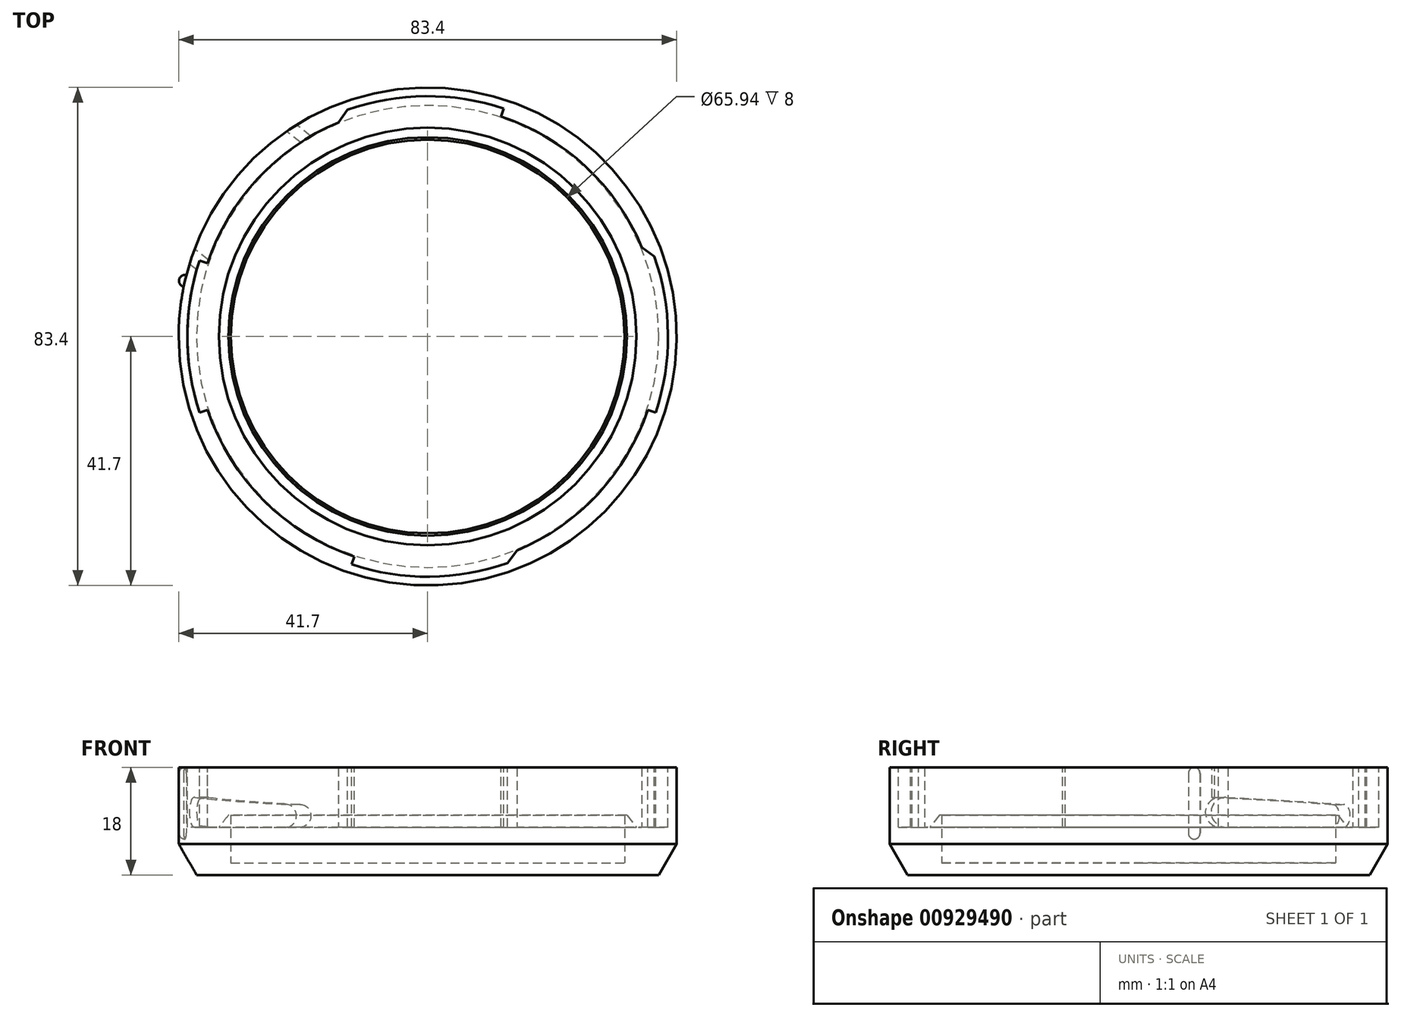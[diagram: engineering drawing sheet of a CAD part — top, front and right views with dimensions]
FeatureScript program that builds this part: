
annotation { "Feature Type Name" : "Feature", "Feature Type Description" : "" }
export const myFeature = defineFeature(function(context is Context, id is Id, definition is map)
    precondition{}
    {
        {
            var Q0;
            Q0=qCreatedBy(makeId("Front.planeOp"),FACE);
            var sketch = newSketch(context, id + "F0", { "sketchPlane" : qUnion([Q0])});
            skLineSegment(sketch, "E0", {"start": v(0, 0) * mm, "end": v(41.7, 0) * mm});
            skLineSegment(sketch, "E1", {"start": v(0, 0) * mm, "end": v(0, 2) * mm});
            skLineSegment(sketch, "E2", {"start": v(41.7, 0) * mm, "end": v(41.7, 18) * mm});
            skLineSegment(sketch, "E3", {"start": v(41.7, 18) * mm, "end": v(38.85, 18) * mm});
            skLineSegment(sketch, "E4", {"start": v(38.85, 18) * mm, "end": v(38.85, 8) * mm});
            skLineSegment(sketch, "E5", {"start": v(38.85, 8) * mm, "end": v(34.97, 8) * mm});
            skLineSegment(sketch, "E6", {"start": v(34.97, 8) * mm, "end": v(34.97, 10) * mm});
            skLineSegment(sketch, "E7", {"start": v(34.97, 10) * mm, "end": v(32.97, 10) * mm});
            skLineSegment(sketch, "E8", {"start": v(32.97, 10) * mm, "end": v(32.97, 2) * mm});
            skLineSegment(sketch, "E9", {"start": v(32.97, 2) * mm, "end": v(0, 2) * mm});
            skLineSegment(sketch, "E10", {"start": v(0, 2) * mm, "end": v(0, 44.08) * mm, "construction": true});
            skSolve(sketch);
        }
        {
            var Q0;
            Q0 = qSketchRegion(id + "F0", true);
            var Q1;
            Q1=sQuery(id+"F0.wireOp",EDGE,"E1");
            revolve(context, id + "F1", {"surfaceOperationType" : NewSurfaceOperationType.NEW, "entities" : qUnion([Q0]), "axis" : qUnion([Q1]), "revolveType" : RevolveType.FULL});
        }
        {
            var Q0;
            Q0=makeQuery(id+"F1.opRevolve","SWEPT_FACE",FACE,{"disambiguationData":[OSD([sQuery(id+"F0.wireOp",EDGE,"E3")])]});
            var sketch = newSketch(context, id + "F2", { "sketchPlane" : qUnion([Q0])});
            skPoint(sketch, "E11.center", {"position": v(0, 0) * mm});
            skArc(sketch, "E12.trimOffspring", {"start": v(12.73, 38.18) * mm, "mid": v(0, 40.25) * mm, "end": v(-12.73, 38.18) * mm});
            skArc(sketch, "E13.1.0", {"start": v(38.18, -12.73) * mm, "mid": v(40.25, 0) * mm, "end": v(38.18, 12.73) * mm});
            skArc(sketch, "E13.2.0", {"start": v(-12.73, -38.18) * mm, "mid": v(0, -40.25) * mm, "end": v(12.73, -38.18) * mm});
            skArc(sketch, "E13.3.0", {"start": v(-38.18, 12.73) * mm, "mid": v(-40.25, 0) * mm, "end": v(-38.18, -12.73) * mm});
            skLineSegment(sketch, "E14", {"start": v(12.73, 38.18) * mm, "end": v(12.29, 36.86) * mm});
            skLineSegment(sketch, "E15", {"start": v(-12.73, 38.18) * mm, "end": v(-12.29, 36.86) * mm});
            skLineSegment(sketch, "E16", {"start": v(38.18, 12.73) * mm, "end": v(36.86, 12.29) * mm});
            skLineSegment(sketch, "E17", {"start": v(38.18, -12.73) * mm, "end": v(36.86, -12.29) * mm});
            skArc(sketch, "E18", {"start": v(12.29, 36.86) * mm, "mid": v(0, 38.85) * mm, "end": v(-12.29, 36.86) * mm});
            skArc(sketch, "E19", {"start": v(-12.29, 36.86) * mm, "mid": v(-27.47, 27.47) * mm, "end": v(-36.86, 12.29) * mm});
            skArc(sketch, "E20", {"start": v(-36.86, 12.29) * mm, "mid": v(-38.85, 0) * mm, "end": v(-36.86, -12.29) * mm});
            skArc(sketch, "E21", {"start": v(-36.86, -12.29) * mm, "mid": v(-27.47, -27.47) * mm, "end": v(-12.29, -36.86) * mm});
            skArc(sketch, "E22", {"start": v(-12.29, -36.86) * mm, "mid": v(0, -38.85) * mm, "end": v(12.29, -36.86) * mm});
            skArc(sketch, "E23", {"start": v(12.29, -36.86) * mm, "mid": v(27.47, -27.47) * mm, "end": v(36.86, -12.29) * mm});
            skArc(sketch, "E24", {"start": v(36.86, -12.29) * mm, "mid": v(38.85, 0) * mm, "end": v(36.86, 12.29) * mm});
            skArc(sketch, "E25", {"start": v(36.86, 12.29) * mm, "mid": v(27.47, 27.47) * mm, "end": v(12.29, 36.86) * mm});
            skLineSegment(sketch, "E26", {"start": v(12.29, -36.86) * mm, "end": v(12.73, -38.18) * mm});
            skLineSegment(sketch, "E27", {"start": v(-12.29, -36.86) * mm, "end": v(-12.73, -38.18) * mm});
            skLineSegment(sketch, "E28", {"start": v(-36.86, -12.29) * mm, "end": v(-38.18, -12.73) * mm});
            skLineSegment(sketch, "E29", {"start": v(-36.86, 12.29) * mm, "end": v(-38.18, 12.73) * mm});
            skSolve(sketch);
        }
        {
            var Q0;
            Q0=makeQuery(id+"F2.imprint","IMPRINT",FACE,{"disambiguationData":[TD([[makeQuery(id+"F2.imprint","IMPRINT",EDGE,{"derivedFrom":sQuery(id+"F2.wireOp",EDGE,"E12.trimOffspring")}),1.0]])]});
            var Q1;
            Q1=makeQuery(id+"F2.imprint","IMPRINT",FACE,{"disambiguationData":[TD([[makeQuery(id+"F2.imprint","IMPRINT",EDGE,{"derivedFrom":sQuery(id+"F2.wireOp",EDGE,"E13.1.0")}),1.0]])]});
            var Q2;
            Q2=makeQuery(id+"F2.imprint","IMPRINT",FACE,{"disambiguationData":[TD([[makeQuery(id+"F2.imprint","IMPRINT",EDGE,{"derivedFrom":sQuery(id+"F2.wireOp",EDGE,"E13.2.0")}),1.0]])]});
            var Q3;
            Q3=makeQuery(id+"F2.imprint","IMPRINT",FACE,{"disambiguationData":[TD([[makeQuery(id+"F2.imprint","IMPRINT",EDGE,{"derivedFrom":sQuery(id+"F2.wireOp",EDGE,"E13.3.0")}),1.0]])]});
            var Q4;
            Q4=makeQuery(id+"F1.opRevolve","SWEPT_FACE",FACE,{"disambiguationData":[OSD([sQuery(id+"F0.wireOp",EDGE,"E5")])]});
            extrude(context, id + "F3", {"entities" : qUnion([Q0, Q1, Q2, Q3]), "operationType" : NewBodyOperationType.REMOVE, "endBound" : BoundingType.UP_TO_SURFACE, "oppositeDirection" : true, "depth" : 10 * mm, "endBoundEntityFace" : qUnion([Q4]), "offsetDistance" : 25 * mm});
        }
        {
            var Q0;
            Q0=makeQuery(id+"F3.boolean.opBoolean","COPY",EDGE,{"derivedFrom":makeQuery(id+"F3.opExtrude","SWEPT_EDGE",EDGE,{"disambiguationData":[OSD([sQuery(id+"F2.wireOp",EDGE,"E16"),sQuery(id+"F2.wireOp",EDGE,"E24"),sQuery(id+"F2.wireOp",EDGE,"E25")])]})});
            var Q1;
            Q1=makeQuery(id+"F3.boolean.opBoolean","COPY",EDGE,{"derivedFrom":makeQuery(id+"F3.opExtrude","SWEPT_EDGE",EDGE,{"disambiguationData":[OSD([sQuery(id+"F2.wireOp",EDGE,"E15"),sQuery(id+"F2.wireOp",EDGE,"E18"),sQuery(id+"F2.wireOp",EDGE,"E19")])]})});
            var Q2;
            Q2=makeQuery(id+"F3.boolean.opBoolean","COPY",EDGE,{"derivedFrom":makeQuery(id+"F3.opExtrude","SWEPT_EDGE",EDGE,{"disambiguationData":[OSD([sQuery(id+"F2.wireOp",EDGE,"E22"),sQuery(id+"F2.wireOp",EDGE,"E23"),sQuery(id+"F2.wireOp",EDGE,"E26")])]})});
            var Q3;
            Q3=makeQuery(id+"F3.boolean.opBoolean","COPY",EDGE,{"derivedFrom":makeQuery(id+"F3.opExtrude","SWEPT_EDGE",EDGE,{"disambiguationData":[OSD([sQuery(id+"F2.wireOp",EDGE,"E20"),sQuery(id+"F2.wireOp",EDGE,"E21"),sQuery(id+"F2.wireOp",EDGE,"E28")])]})});
            chamfer(context, id + "F4", {"entities" : qUnion([Q0, Q1, Q2, Q3]), "chamferType" : ChamferType.TWO_OFFSETS, "width1" : 3 * mm, "oppositeDirection" : false, "width2" : 2 * mm, "tangentPropagation" : true});
        }
        {
            var Q0;
            Q0=makeQuery(id+"F1.opRevolve","SWEPT_EDGE",EDGE,{"disambiguationData":[OSD([sQuery(id+"F0.wireOp",EDGE,"E6"),sQuery(id+"F0.wireOp",EDGE,"E7")])]});
            chamfer(context, id + "F5", {"entities" : qUnion([Q0]), "chamferType" : ChamferType.TWO_OFFSETS, "width1" : 2 * mm, "oppositeDirection" : false, "width2" : 1.6 * mm, "tangentPropagation" : true});
        }
        {
            var Q0;
            Q0=sQuery(id+"F0.wireOp",EDGE,"E10");
            cPlane(context, id + "F6", {"entities" : qUnion([Q0]), "cplaneType" : CPlaneType.LINE_ANGLE, "offset" : 25 * mm, "angle" : 38 * degree, "oppositeDirection" : true, "width" : 150 * mm, "height" : 150 * mm});
        }
        {
            var Q0;
            Q0=qCreatedBy(id+"F6.planeOp",FACE);
            cPlane(context, id + "F7", {"entities" : qUnion([Q0]), "cplaneType" : CPlaneType.OFFSET, "offset" : 50 * mm, "oppositeDirection" : true, "width" : 150 * mm, "height" : 150 * mm});
        }
        {
            var Q0;
            Q0=qCreatedBy(id+"F7.planeOp",FACE);
            var sketch = newSketch(context, id + "F8", { "sketchPlane" : qUnion([Q0])});
            skLineSegment(sketch, "E30.0", {"start": v(23.92, 8) * mm, "end": v(21.53, 8) * mm});
            skLineSegment(sketch, "E31", {"start": v(0, 8) * mm, "end": v(-12.5, 8) * mm});
            skLineSegment(sketch, "E32.MirrorCS", {"start": v(0, 8) * mm, "end": v(12.5, 8) * mm});
            skArc(sketch, "E33", {"start": v(12.5, 8) * mm, "mid": v(14.4, 9.9) * mm, "end": v(12.5, 11.8) * mm});
            skArc(sketch, "E34", {"start": v(-12.5, 13) * mm, "mid": v(-15, 10.5) * mm, "end": v(-12.5, 8) * mm});
            skLineSegment(sketch, "E35", {"start": v(12.5, 11.8) * mm, "end": v(-12.5, 13) * mm});
            skSolve(sketch);
        }
        {
            var Q0;
            Q0=makeQuery(id+"F8.imprint","IMPRINT",FACE,{"disambiguationData":[TD([[makeQuery(id+"F8.imprint","IMPRINT",EDGE,{"derivedFrom":sQuery(id+"F8.wireOp",EDGE,"E31")}),-1.0]])]});
            extrude(context, id + "F9", {"entities" : qUnion([Q0]), "operationType" : NewBodyOperationType.REMOVE, "depth" : 14.8 * mm, "offsetDistance" : 25 * mm});
        }
        {
            var Q0;
            Q0=makeQuery(id+"F1.opRevolve","SWEPT_EDGE",EDGE,{"disambiguationData":[OSD([sQuery(id+"F0.wireOp",EDGE,"E0"),sQuery(id+"F0.wireOp",EDGE,"E2")])]});
            chamfer(context, id + "F10", {"entities" : qUnion([Q0]), "chamferType" : ChamferType.OFFSET_ANGLE, "width" : 3 * mm, "oppositeDirection" : false, "angle" : 60 * degree, "tangentPropagation" : true});
        }
        {
            var Q0;
            Q0=qCreatedBy(makeId("Top.planeOp"),FACE);
            cPlane(context, id + "F11", {"entities" : qUnion([Q0]), "cplaneType" : CPlaneType.OFFSET, "offset" : 6 * mm, "width" : 150 * mm, "height" : 150 * mm});
        }
        {
            var Q0;
            Q0=qCreatedBy(id+"F11.planeOp",FACE);
            var sketch = newSketch(context, id + "F12", { "sketchPlane" : qUnion([Q0])});
            skCircle(sketch, "E36", {"center": v(-40.65, 9.31) * mm, "radius": 1 * mm});
            skSolve(sketch);
        }
        {
            var Q0;
            Q0 = qSketchRegion(id + "F12", true);
            var Q1;
            Q1=makeQuery(id+"F1.opRevolve","SWEPT_FACE",FACE,{"disambiguationData":[OSD([sQuery(id+"F0.wireOp",EDGE,"E3")])]});
            extrude(context, id + "F13", {"entities" : qUnion([Q0]), "operationType" : NewBodyOperationType.ADD, "endBound" : BoundingType.UP_TO_SURFACE, "depth" : 12 * mm, "endBoundEntityFace" : qUnion([Q1]), "offsetDistance" : 25 * mm});
        }
        {
            var Q0;
            Q0=makeQuery(id+"F13.opExtrude","CAP_EDGE",EDGE,{"disambiguationData":[OSD([sQuery(id+"F12.wireOp",EDGE,"E36")])],"isStart":true});
            var Q1;
            Q1=makeQuery(id+"F13.opExtrude","CAP_EDGE",EDGE,{"disambiguationData":[OSD([sQuery(id+"F12.wireOp",EDGE,"E36")])],"isStart":false});
            fillet(context, id + "F14", {"entities" : qUnion([Q0, Q1]), "radius" : 1 * mm, "tangentPropagation" : true, "allowEdgeOverflow" : false});
        }
    });
